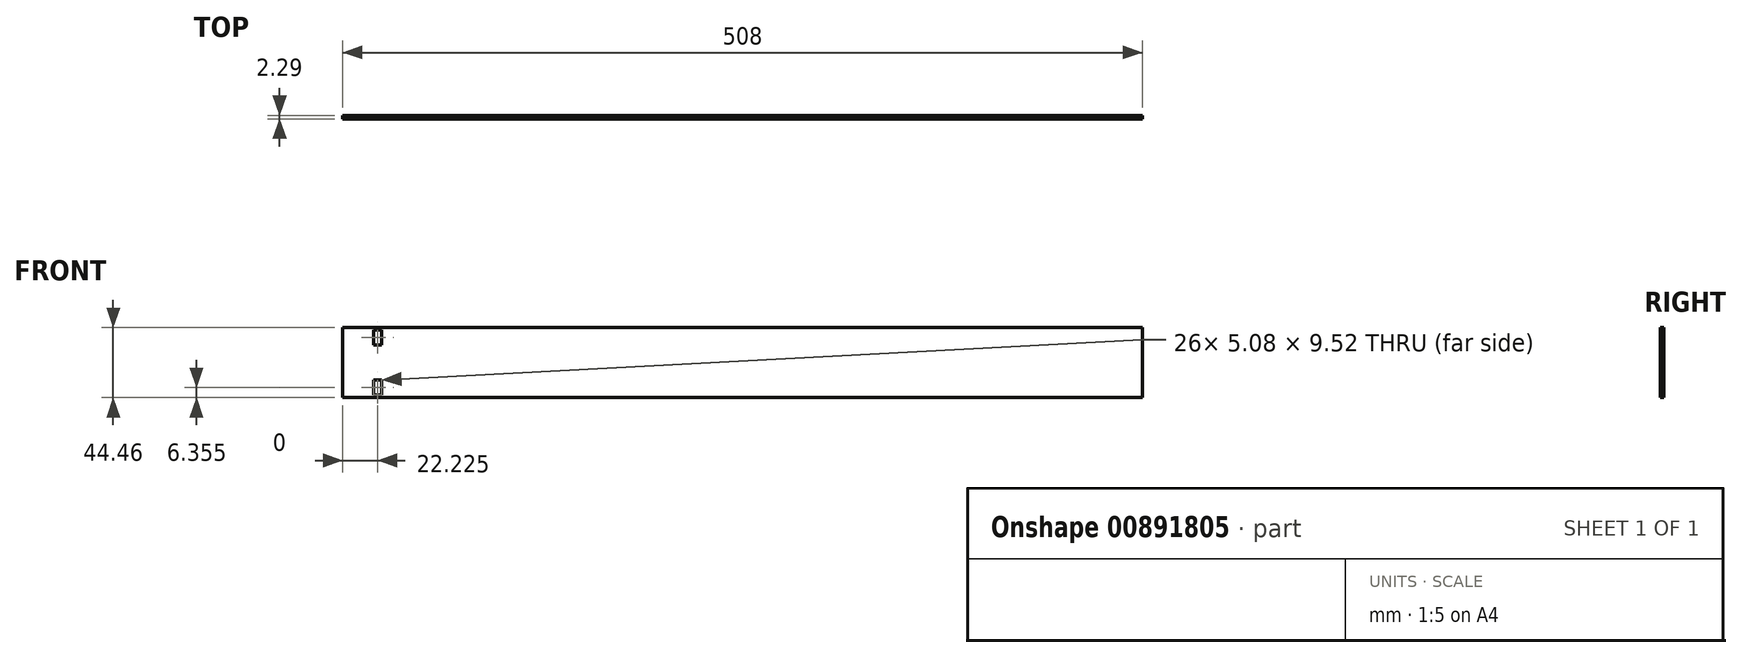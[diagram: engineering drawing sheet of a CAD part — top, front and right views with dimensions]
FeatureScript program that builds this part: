
annotation { "Feature Type Name" : "Feature", "Feature Type Description" : "" }
export const myFeature = defineFeature(function(context is Context, id is Id, definition is map)
    precondition{}
    {
        {
            var Q0;
            Q0=qCreatedBy(makeId("Front.planeOp"),FACE);
            var sketch = newSketch(context, id + "F0", { "sketchPlane" : qUnion([Q0])});
            skLineSegment(sketch, "E0.bottom", {"start": v(-254, 22.23) * mm, "end": v(254, 22.23) * mm});
            skLineSegment(sketch, "E0.top", {"start": v(-254, -22.23) * mm, "end": v(254, -22.23) * mm});
            skLineSegment(sketch, "E0.left", {"start": v(-254, 22.23) * mm, "end": v(-254, -22.23) * mm});
            skLineSegment(sketch, "E0.right", {"start": v(254, 22.23) * mm, "end": v(254, -22.23) * mm});
            skLineSegment(sketch, "E1", {"start": v(-254, 22.23) * mm, "end": v(254, -22.23) * mm, "construction": true});
            skSolve(sketch);
        }
        {
            var Q0;
            Q0 = qSketchRegion(id + "F0", true);
            extrude(context, id + "F1", {"entities" : qUnion([Q0]), "depth" : 2.3 * mm, "offsetDistance" : 25.4 * mm});
        }
        {
            var Q0;
            Q0=makeQuery(id+"F1.opExtrude","CAP_FACE",FACE,{"disambiguationData":[OSD([sQuery(id+"F0.wireOp",EDGE,"E0.bottom"),sQuery(id+"F0.wireOp",EDGE,"E0.top"),sQuery(id+"F0.wireOp",EDGE,"E0.left"),sQuery(id+"F0.wireOp",EDGE,"E0.right")])],"isStart":false});
            var sketch = newSketch(context, id + "F2", { "sketchPlane" : qUnion([Q0])});
            skLineSegment(sketch, "E2.bottom", {"start": v(-229.24, 20.64) * mm, "end": v(-234.32, 20.64) * mm});
            skLineSegment(sketch, "E2.top", {"start": v(-229.24, 11.11) * mm, "end": v(-234.32, 11.11) * mm});
            skLineSegment(sketch, "E2.left", {"start": v(-229.24, 20.64) * mm, "end": v(-229.24, 11.11) * mm});
            skLineSegment(sketch, "E2.right", {"start": v(-234.32, 20.64) * mm, "end": v(-234.32, 11.11) * mm});
            skPoint(sketch, "E2.middle", {"position": v(-231.78, 15.87) * mm});
            skLineSegment(sketch, "E3.bottom", {"start": v(-234.32, -11.11) * mm, "end": v(-229.24, -11.11) * mm});
            skLineSegment(sketch, "E3.top", {"start": v(-234.32, -20.64) * mm, "end": v(-229.24, -20.64) * mm});
            skLineSegment(sketch, "E3.left", {"start": v(-234.32, -11.11) * mm, "end": v(-234.32, -20.64) * mm});
            skLineSegment(sketch, "E3.right", {"start": v(-229.24, -11.11) * mm, "end": v(-229.24, -20.64) * mm});
            skLineSegment(sketch, "E4", {"start": v(-234.32, -11.11) * mm, "end": v(-229.24, -20.64) * mm, "construction": true});
            skPoint(sketch, "E5", {"position": v(-231.78, -15.88) * mm});
            skSolve(sketch);
        }
        {
            var Q0;
            Q0 = qSketchRegion(id + "F2", true);
            extrude(context, id + "F3", {"entities" : qUnion([Q0]), "operationType" : NewBodyOperationType.REMOVE, "endBound" : BoundingType.THROUGH_ALL, "oppositeDirection" : true, "depth" : 25.4 * mm, "offsetDistance" : 25.4 * mm});
        }
    });
